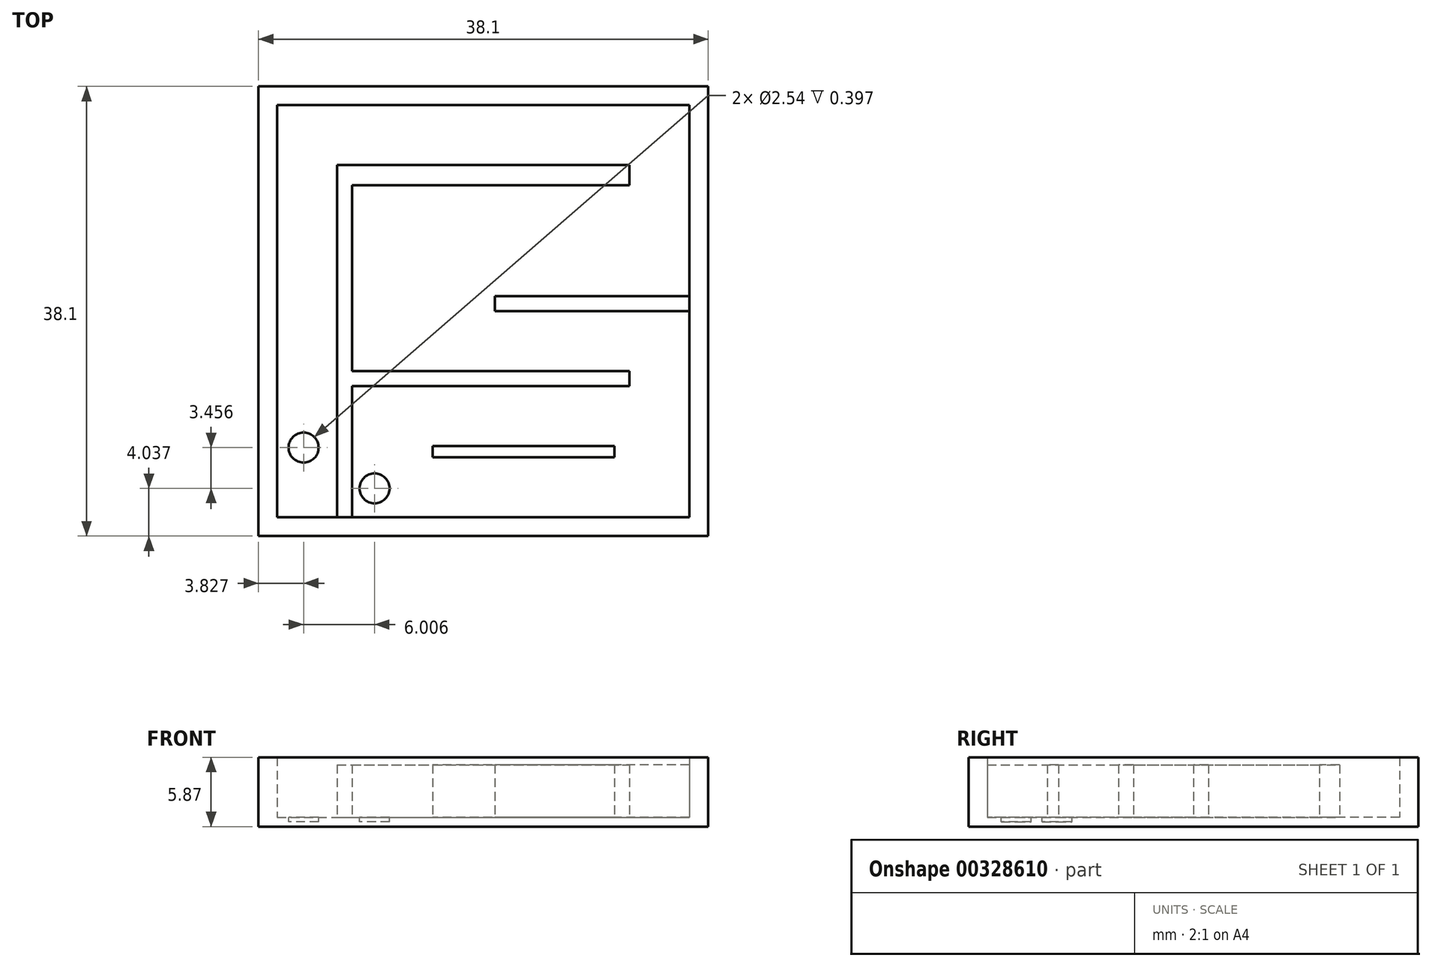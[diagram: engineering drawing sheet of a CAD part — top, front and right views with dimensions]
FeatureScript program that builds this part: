
annotation { "Feature Type Name" : "Feature", "Feature Type Description" : "" }
export const myFeature = defineFeature(function(context is Context, id is Id, definition is map)
    precondition{}
    {
        {
            var Q0;
            Q0=qCreatedBy(makeId("Top.planeOp"),FACE);
            var sketch = newSketch(context, id + "F0", { "sketchPlane" : qUnion([Q0])});
            skLineSegment(sketch, "E0.bottom", {"start": v(-24.4, 15.61) * mm, "end": v(13.7, 15.61) * mm});
            skLineSegment(sketch, "E0.top", {"start": v(-24.4, -22.49) * mm, "end": v(13.7, -22.49) * mm});
            skLineSegment(sketch, "E0.left", {"start": v(-24.4, 15.61) * mm, "end": v(-24.4, -22.49) * mm});
            skLineSegment(sketch, "E0.right", {"start": v(13.7, 15.61) * mm, "end": v(13.7, -22.49) * mm});
            skSolve(sketch);
        }
        {
            var Q0;
            Q0=makeQuery(id+"F0.imprint","IMPRINT",FACE,{"disambiguationData":[TD([[makeQuery(id+"F0.imprint","IMPRINT",EDGE,{"derivedFrom":sQuery(id+"F0.wireOp",EDGE,"E0.bottom")}),-1.0]])]});
            extrude(context, id + "F1", {"entities" : qUnion([Q0]), "depth" : 0.8 * mm});
        }
        {
            var Q0;
            Q0=makeQuery(id+"F1.opExtrude","CAP_FACE",FACE,{"disambiguationData":[OSD([sQuery(id+"F0.wireOp",EDGE,"E0.bottom"),sQuery(id+"F0.wireOp",EDGE,"E0.top"),sQuery(id+"F0.wireOp",EDGE,"E0.left"),sQuery(id+"F0.wireOp",EDGE,"E0.right")])],"isStart":false});
            var sketch = newSketch(context, id + "F2", { "sketchPlane" : qUnion([Q0])});
            skLineSegment(sketch, "E1.0", {"start": v(-22.81, 14.03) * mm, "end": v(12.11, 14.03) * mm});
            skLineSegment(sketch, "E1.1", {"start": v(-22.81, 14.03) * mm, "end": v(-22.81, -20.9) * mm});
            skLineSegment(sketch, "E1.2", {"start": v(-22.81, -20.9) * mm, "end": v(12.11, -20.9) * mm});
            skLineSegment(sketch, "E1.3", {"start": v(12.11, 14.03) * mm, "end": v(12.11, -20.9) * mm});
            skSolve(sketch);
        }
        {
            var Q0;
            Q0=makeQuery(id+"F2.imprint","IMPRINT",FACE,{"disambiguationData":[TD([[makeQuery(id+"F2.imprint","IMPRINT",EDGE,{"derivedFrom":sQuery(id+"F2.wireOp",EDGE,"E1.0")}),1.0]])]});
            extrude(context, id + "F3", {"entities" : qUnion([Q0]), "operationType" : NewBodyOperationType.ADD, "depth" : 5.08 * mm});
        }
        {
            var Q0;
            Q0=makeQuery(id+"F1.opExtrude","CAP_FACE",FACE,{"disambiguationData":[OSD([sQuery(id+"F0.wireOp",EDGE,"E0.bottom"),sQuery(id+"F0.wireOp",EDGE,"E0.top"),sQuery(id+"F0.wireOp",EDGE,"E0.left"),sQuery(id+"F0.wireOp",EDGE,"E0.right")])],"isStart":false});
            var sketch = newSketch(context, id + "F4", { "sketchPlane" : qUnion([Q0])});
            skLineSegment(sketch, "E2.bottom", {"start": v(-17.73, -20.9) * mm, "end": v(-16.46, -20.9) * mm});
            skLineSegment(sketch, "E2.top", {"start": v(-17.73, 8.95) * mm, "end": v(-16.46, 8.95) * mm});
            skLineSegment(sketch, "E2.left", {"start": v(-16.46, -20.9) * mm, "end": v(-16.46, 8.95) * mm});
            skLineSegment(sketch, "E2.right", {"start": v(-17.73, -20.9) * mm, "end": v(-17.73, 8.95) * mm});
            skLineSegment(sketch, "E3.bottom", {"start": v(12.11, -3.44) * mm, "end": v(-4.39, -3.44) * mm});
            skLineSegment(sketch, "E3.top", {"start": v(12.11, -2.17) * mm, "end": v(-4.39, -2.17) * mm});
            skLineSegment(sketch, "E3.left", {"start": v(12.11, -3.44) * mm, "end": v(12.11, -2.17) * mm});
            skLineSegment(sketch, "E3.right", {"start": v(-4.39, -3.44) * mm, "end": v(-4.39, -2.17) * mm});
            skLineSegment(sketch, "E4.bottom", {"start": v(-16.46, 8.95) * mm, "end": v(7.03, 8.95) * mm});
            skLineSegment(sketch, "E4.top", {"start": v(-16.46, 7.22) * mm, "end": v(7.03, 7.22) * mm});
            skLineSegment(sketch, "E4.left", {"start": v(-16.46, 8.95) * mm, "end": v(-16.46, 7.22) * mm});
            skLineSegment(sketch, "E4.right", {"start": v(7.03, 8.95) * mm, "end": v(7.03, 7.22) * mm});
            skLineSegment(sketch, "E5.bottom", {"start": v(-16.46, -8.52) * mm, "end": v(-9.47, -8.52) * mm});
            skLineSegment(sketch, "E5.top", {"start": v(-16.46, -9.79) * mm, "end": v(-9.47, -9.79) * mm});
            skLineSegment(sketch, "E5.left", {"start": v(-16.46, -8.52) * mm, "end": v(-16.46, -9.79) * mm});
            skLineSegment(sketch, "E5.right", {"start": v(-9.47, -8.52) * mm, "end": v(-9.47, -9.79) * mm});
            skLineSegment(sketch, "E6.bottom", {"start": v(-9.47, -8.52) * mm, "end": v(-11.38, -8.52) * mm});
            skLineSegment(sketch, "E6.top", {"start": v(-9.47, 2.14) * mm, "end": v(-11.38, 2.14) * mm});
            skLineSegment(sketch, "E6.left", {"start": v(-9.47, -8.52) * mm, "end": v(-9.47, 2.14) * mm});
            skLineSegment(sketch, "E6.right", {"start": v(-11.38, -8.52) * mm, "end": v(-11.38, 2.14) * mm});
            skLineSegment(sketch, "E7.bottom", {"start": v(-9.47, -8.52) * mm, "end": v(7.03, -8.52) * mm});
            skLineSegment(sketch, "E7.top", {"start": v(-9.47, -9.79) * mm, "end": v(7.03, -9.79) * mm});
            skLineSegment(sketch, "E7.right", {"start": v(7.03, -8.52) * mm, "end": v(7.03, -9.79) * mm});
            skLineSegment(sketch, "E8.bottom", {"start": v(7.03, -9.79) * mm, "end": v(5.76, -9.79) * mm});
            skLineSegment(sketch, "E8.top", {"start": v(7.03, -15.82) * mm, "end": v(5.76, -15.82) * mm});
            skLineSegment(sketch, "E8.left", {"start": v(7.03, -9.79) * mm, "end": v(7.03, -15.82) * mm});
            skLineSegment(sketch, "E8.right", {"start": v(5.76, -9.79) * mm, "end": v(5.76, -15.82) * mm});
            skLineSegment(sketch, "E9.bottom", {"start": v(5.76, -15.82) * mm, "end": v(-9.63, -15.82) * mm});
            skLineSegment(sketch, "E9.top", {"start": v(5.76, -14.87) * mm, "end": v(-9.63, -14.87) * mm});
            skLineSegment(sketch, "E9.left", {"start": v(5.76, -15.82) * mm, "end": v(5.76, -14.87) * mm});
            skLineSegment(sketch, "E9.right", {"start": v(-9.63, -15.82) * mm, "end": v(-9.63, -14.87) * mm});
            skCircle(sketch, "E10", {"center": v(-20.57, -15) * mm, "radius": 1.27 * mm});
            skCircle(sketch, "E11", {"center": v(-14.57, -18.45) * mm, "radius": 1.27 * mm});
            skSolve(sketch);
        }
        {
            var Q0;
            {var subQ3=sQuery(id+"F4.wireOp",EDGE,"E2.bottom");Q0=makeQuery(id+"F4.imprint","IMPRINT",FACE,{"disambiguationData":[TD([[makeQuery(id+"F4.imprint","IMPRINT",EDGE,{"derivedFrom":subQ3}),1.0]])]});}
            var Q1;
            Q1=makeQuery(id+"F4.imprint","IMPRINT",FACE,{"disambiguationData":[TD([[makeQuery(id+"F4.imprint","IMPRINT",EDGE,{"derivedFrom":sQuery(id+"F4.wireOp",EDGE,"E4.bottom")}),-1.0]])]});
            var Q2;
            Q2=makeQuery(id+"F4.imprint","IMPRINT",FACE,{"disambiguationData":[TD([[makeQuery(id+"F4.imprint","IMPRINT",EDGE,{"derivedFrom":sQuery(id+"F4.wireOp",EDGE,"E6.bottom")}),-1.0]])]});
            var Q3;
            Q3=makeQuery(id+"F4.imprint","IMPRINT",FACE,{"disambiguationData":[TD([[makeQuery(id+"F4.imprint","IMPRINT",EDGE,{"derivedFrom":sQuery(id+"F4.wireOp",EDGE,"E5.bottom")}),-1.0]])]});
            var Q4;
            Q4=makeQuery(id+"F4.imprint","IMPRINT",FACE,{"disambiguationData":[TD([[makeQuery(id+"F4.imprint","IMPRINT",EDGE,{"derivedFrom":sQuery(id+"F4.wireOp",EDGE,"E7.bottom")}),-1.0]])]});
            var Q5;
            Q5=makeQuery(id+"F4.imprint","IMPRINT",FACE,{"disambiguationData":[TD([[makeQuery(id+"F4.imprint","IMPRINT",EDGE,{"derivedFrom":sQuery(id+"F4.wireOp",EDGE,"E3.bottom")}),-1.0]])]});
            var Q6;
            Q6=makeQuery(id+"F4.imprint","IMPRINT",FACE,{"disambiguationData":[TD([[makeQuery(id+"F4.imprint","IMPRINT",EDGE,{"derivedFrom":sQuery(id+"F4.wireOp",EDGE,"E8.bottom")}),1.0]])]});
            var Q7;
            Q7=makeQuery(id+"F4.imprint","IMPRINT",FACE,{"disambiguationData":[TD([[makeQuery(id+"F4.imprint","IMPRINT",EDGE,{"derivedFrom":sQuery(id+"F4.wireOp",EDGE,"E9.bottom")}),-1.0]])]});
            extrude(context, id + "F5", {"entities" : qUnion([Q0, Q1, Q2, Q3, Q4, Q5, Q6, Q7]), "operationType" : NewBodyOperationType.ADD, "depth" : 4.44 * mm});
        }
        {
            var Q0;
            Q0=makeQuery(id+"F4.imprint","IMPRINT",FACE,{"disambiguationData":[TD([[makeQuery(id+"F4.imprint","IMPRINT",EDGE,{"derivedFrom":sQuery(id+"F4.wireOp",EDGE,"E10")}),1.0]])]});
            var Q1;
            Q1=makeQuery(id+"F4.imprint","IMPRINT",FACE,{"disambiguationData":[TD([[makeQuery(id+"F4.imprint","IMPRINT",EDGE,{"derivedFrom":sQuery(id+"F4.wireOp",EDGE,"E11")}),1.0]])]});
            extrude(context, id + "F6", {"entities" : qUnion([Q0, Q1]), "operationType" : NewBodyOperationType.REMOVE, "oppositeDirection" : true, "depth" : 0.4 * mm});
        }
    });
